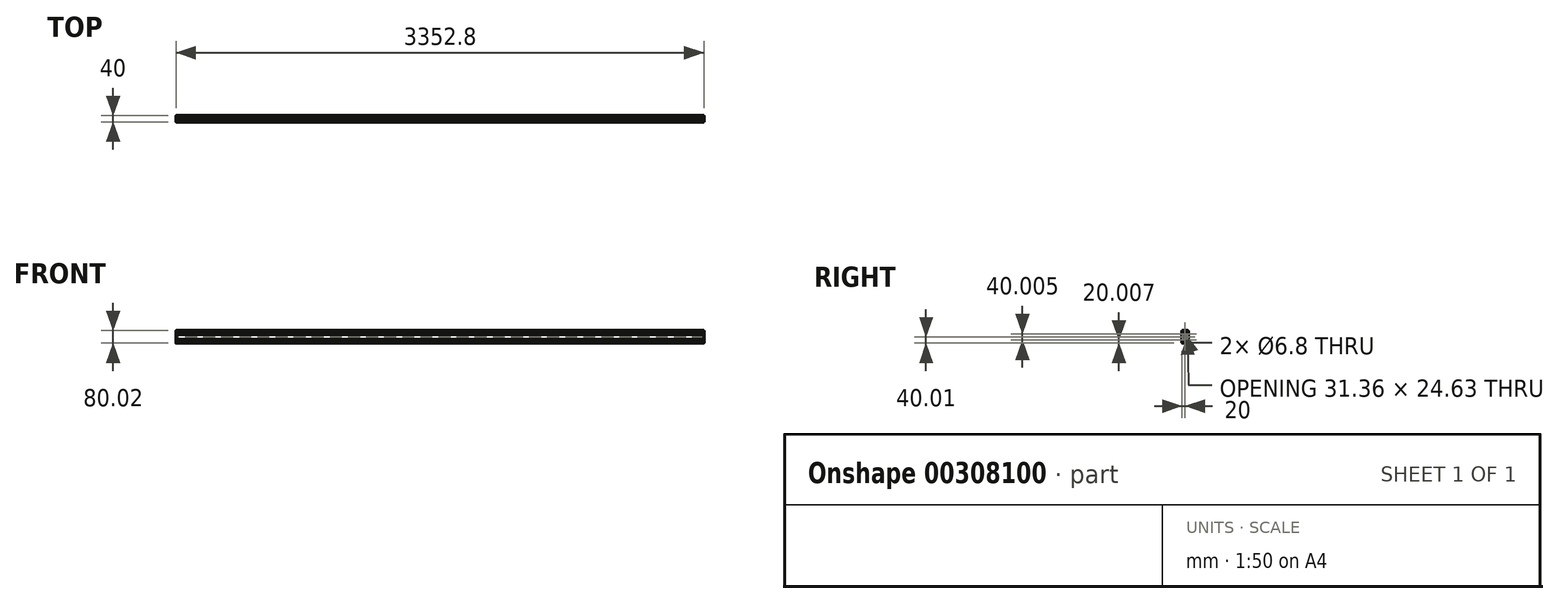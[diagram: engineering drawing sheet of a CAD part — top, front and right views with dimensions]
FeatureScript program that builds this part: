
annotation { "Feature Type Name" : "Feature", "Feature Type Description" : "" }
export const myFeature = defineFeature(function(context is Context, id is Id, definition is map)
    precondition{}
    {
        {
            var Q0;
            Q0=qCreatedBy(makeId("Right.planeOp"),FACE);
            var sketch = newSketch(context, id + "F0", { "sketchPlane" : qUnion([Q0])});
            skLineSegment(sketch, "E0", {"start": v(-3.57, -20) * mm, "end": v(3.57, -20) * mm});
            skLineSegment(sketch, "E1", {"start": v(0, -23.57) * mm, "end": v(0, -16.43) * mm});
            skLineSegment(sketch, "E2", {"start": v(-3.57, 20) * mm, "end": v(3.57, 20) * mm});
            skLineSegment(sketch, "E3", {"start": v(0, 16.43) * mm, "end": v(0, 23.57) * mm});
            skArc(sketch, "E4", {"start": v(-16.83, 40) * mm, "mid": v(-19.07, 39.08) * mm, "end": v(-20, 36.83) * mm});
            skLineSegment(sketch, "E5", {"start": v(-20, 36.83) * mm, "end": v(-20, 25.7) * mm});
            skArc(sketch, "E6", {"start": v(-20, 25.7) * mm, "mid": v(-19.54, 24.58) * mm, "end": v(-18.43, 24.12) * mm});
            skLineSegment(sketch, "E7", {"start": v(-18.43, 24.12) * mm, "end": v(-17.25, 24.12) * mm});
            skArc(sketch, "E8", {"start": v(-17.25, 24.12) * mm, "mid": v(-16.14, 24.58) * mm, "end": v(-15.68, 25.7) * mm});
            skLineSegment(sketch, "E9", {"start": v(-15.68, 25.7) * mm, "end": v(-15.68, 28.72) * mm});
            skArc(sketch, "E10", {"start": v(-14.11, 30.29) * mm, "mid": v(-15.22, 29.83) * mm, "end": v(-15.68, 28.72) * mm});
            skLineSegment(sketch, "E11", {"start": v(-14.11, 30.29) * mm, "end": v(-13.66, 30.29) * mm});
            skArc(sketch, "E12", {"start": v(-13.12, 30.07) * mm, "mid": v(-13.37, 30.23) * mm, "end": v(-13.66, 30.29) * mm});
            skLineSegment(sketch, "E13", {"start": v(-13.12, 30.07) * mm, "end": v(-9.11, 26.06) * mm});
            skArc(sketch, "E14", {"start": v(-7.69, 22.62) * mm, "mid": v(-8.06, 24.48) * mm, "end": v(-9.11, 26.06) * mm});
            skLineSegment(sketch, "E15", {"start": v(-7.69, 22.62) * mm, "end": v(-7.69, 17.39) * mm});
            skArc(sketch, "E16", {"start": v(-9.11, 13.95) * mm, "mid": v(-8.06, 15.53) * mm, "end": v(-7.69, 17.39) * mm});
            skLineSegment(sketch, "E17", {"start": v(-9.11, 13.95) * mm, "end": v(-13.12, 9.94) * mm});
            skArc(sketch, "E18", {"start": v(-13.66, 9.72) * mm, "mid": v(-13.37, 9.77) * mm, "end": v(-13.12, 9.94) * mm});
            skLineSegment(sketch, "E19", {"start": v(-13.66, 9.72) * mm, "end": v(-14.11, 9.72) * mm});
            skArc(sketch, "E20", {"start": v(-15.68, 11.29) * mm, "mid": v(-15.22, 10.18) * mm, "end": v(-14.11, 9.72) * mm});
            skLineSegment(sketch, "E21", {"start": v(-15.68, 11.29) * mm, "end": v(-15.68, 14.31) * mm});
            skArc(sketch, "E22", {"start": v(-15.68, 14.31) * mm, "mid": v(-16.14, 15.42) * mm, "end": v(-17.25, 15.88) * mm});
            skLineSegment(sketch, "E23", {"start": v(-17.25, 15.88) * mm, "end": v(-18.43, 15.88) * mm});
            skArc(sketch, "E24", {"start": v(-18.43, 15.88) * mm, "mid": v(-19.54, 15.42) * mm, "end": v(-20, 14.31) * mm});
            skLineSegment(sketch, "E25", {"start": v(-20, 14.31) * mm, "end": v(-20, -14.31) * mm});
            skArc(sketch, "E26", {"start": v(-20, -14.31) * mm, "mid": v(-19.54, -15.42) * mm, "end": v(-18.43, -15.88) * mm});
            skLineSegment(sketch, "E27", {"start": v(-18.43, -15.88) * mm, "end": v(-17.25, -15.88) * mm});
            skArc(sketch, "E28", {"start": v(-17.25, -15.88) * mm, "mid": v(-16.14, -15.42) * mm, "end": v(-15.68, -14.31) * mm});
            skLineSegment(sketch, "E29", {"start": v(-15.68, -14.31) * mm, "end": v(-15.68, -11.29) * mm});
            skArc(sketch, "E30", {"start": v(-14.11, -9.72) * mm, "mid": v(-15.22, -10.18) * mm, "end": v(-15.68, -11.29) * mm});
            skLineSegment(sketch, "E31", {"start": v(-14.11, -9.72) * mm, "end": v(-13.66, -9.72) * mm});
            skArc(sketch, "E32", {"start": v(-13.12, -9.94) * mm, "mid": v(-13.37, -9.77) * mm, "end": v(-13.66, -9.72) * mm});
            skLineSegment(sketch, "E33", {"start": v(-13.12, -9.94) * mm, "end": v(-9.11, -13.95) * mm});
            skArc(sketch, "E34", {"start": v(-7.69, -17.39) * mm, "mid": v(-8.06, -15.53) * mm, "end": v(-9.11, -13.95) * mm});
            skLineSegment(sketch, "E35", {"start": v(-7.69, -17.39) * mm, "end": v(-7.69, -22.62) * mm});
            skArc(sketch, "E36", {"start": v(-9.11, -26.06) * mm, "mid": v(-8.06, -24.48) * mm, "end": v(-7.69, -22.62) * mm});
            skLineSegment(sketch, "E37", {"start": v(-9.11, -26.06) * mm, "end": v(-13.12, -30.07) * mm});
            skArc(sketch, "E38", {"start": v(-13.66, -30.29) * mm, "mid": v(-13.37, -30.23) * mm, "end": v(-13.12, -30.07) * mm});
            skLineSegment(sketch, "E39", {"start": v(-13.66, -30.29) * mm, "end": v(-14.11, -30.29) * mm});
            skArc(sketch, "E40", {"start": v(-15.68, -28.72) * mm, "mid": v(-15.22, -29.83) * mm, "end": v(-14.11, -30.29) * mm});
            skLineSegment(sketch, "E41", {"start": v(-15.68, -28.72) * mm, "end": v(-15.68, -25.7) * mm});
            skArc(sketch, "E42", {"start": v(-15.68, -25.7) * mm, "mid": v(-16.14, -24.58) * mm, "end": v(-17.25, -24.12) * mm});
            skLineSegment(sketch, "E43", {"start": v(-17.25, -24.12) * mm, "end": v(-18.43, -24.12) * mm});
            skArc(sketch, "E44", {"start": v(-18.43, -24.12) * mm, "mid": v(-19.54, -24.58) * mm, "end": v(-20, -25.7) * mm});
            skLineSegment(sketch, "E45", {"start": v(-20, -25.7) * mm, "end": v(-20, -36.83) * mm});
            skArc(sketch, "E46", {"start": v(-20, -36.83) * mm, "mid": v(-19.07, -39.08) * mm, "end": v(-16.83, -40) * mm});
            skLineSegment(sketch, "E47", {"start": v(-16.83, -40) * mm, "end": v(-5.7, -40) * mm});
            skArc(sketch, "E48", {"start": v(-5.7, -40) * mm, "mid": v(-4.58, -39.55) * mm, "end": v(-4.12, -38.43) * mm});
            skLineSegment(sketch, "E49", {"start": v(-4.12, -38.43) * mm, "end": v(-4.12, -37.25) * mm});
            skArc(sketch, "E50", {"start": v(-4.12, -37.25) * mm, "mid": v(-4.58, -36.14) * mm, "end": v(-5.7, -35.68) * mm});
            skLineSegment(sketch, "E51", {"start": v(-5.7, -35.68) * mm, "end": v(-8.72, -35.68) * mm});
            skArc(sketch, "E52", {"start": v(-10.29, -34.11) * mm, "mid": v(-9.83, -35.22) * mm, "end": v(-8.72, -35.68) * mm});
            skLineSegment(sketch, "E53", {"start": v(-10.29, -34.11) * mm, "end": v(-10.29, -33.66) * mm});
            skArc(sketch, "E54", {"start": v(-10.06, -33.12) * mm, "mid": v(-10.23, -33.37) * mm, "end": v(-10.29, -33.66) * mm});
            skLineSegment(sketch, "E55", {"start": v(-10.06, -33.12) * mm, "end": v(-6.06, -29.11) * mm});
            skArc(sketch, "E56", {"start": v(-2.62, -27.69) * mm, "mid": v(-4.48, -28.06) * mm, "end": v(-6.06, -29.11) * mm});
            skLineSegment(sketch, "E57", {"start": v(-2.62, -27.69) * mm, "end": v(2.62, -27.69) * mm});
            skArc(sketch, "E58", {"start": v(6.06, -29.11) * mm, "mid": v(4.48, -28.06) * mm, "end": v(2.62, -27.69) * mm});
            skLineSegment(sketch, "E59", {"start": v(6.06, -29.11) * mm, "end": v(10.06, -33.12) * mm});
            skArc(sketch, "E60", {"start": v(10.29, -33.66) * mm, "mid": v(10.23, -33.37) * mm, "end": v(10.06, -33.12) * mm});
            skLineSegment(sketch, "E61", {"start": v(10.29, -33.66) * mm, "end": v(10.29, -34.11) * mm});
            skArc(sketch, "E62", {"start": v(8.72, -35.68) * mm, "mid": v(9.83, -35.22) * mm, "end": v(10.29, -34.11) * mm});
            skLineSegment(sketch, "E63", {"start": v(8.72, -35.68) * mm, "end": v(5.7, -35.68) * mm});
            skArc(sketch, "E64", {"start": v(5.7, -35.68) * mm, "mid": v(4.58, -36.14) * mm, "end": v(4.12, -37.25) * mm});
            skLineSegment(sketch, "E65", {"start": v(4.12, -37.25) * mm, "end": v(4.12, -38.43) * mm});
            skArc(sketch, "E66", {"start": v(4.12, -38.43) * mm, "mid": v(4.58, -39.55) * mm, "end": v(5.7, -40) * mm});
            skLineSegment(sketch, "E67", {"start": v(5.7, -40) * mm, "end": v(16.83, -40) * mm});
            skArc(sketch, "E68", {"start": v(16.83, -40) * mm, "mid": v(19.07, -39.08) * mm, "end": v(20, -36.83) * mm});
            skLineSegment(sketch, "E69", {"start": v(20, -36.83) * mm, "end": v(20, -25.7) * mm});
            skArc(sketch, "E70", {"start": v(20, -25.7) * mm, "mid": v(19.54, -24.58) * mm, "end": v(18.43, -24.12) * mm});
            skLineSegment(sketch, "E71", {"start": v(18.43, -24.12) * mm, "end": v(17.25, -24.12) * mm});
            skArc(sketch, "E72", {"start": v(17.25, -24.12) * mm, "mid": v(16.14, -24.58) * mm, "end": v(15.68, -25.7) * mm});
            skLineSegment(sketch, "E73", {"start": v(15.68, -25.7) * mm, "end": v(15.68, -28.72) * mm});
            skArc(sketch, "E74", {"start": v(14.11, -30.29) * mm, "mid": v(15.22, -29.83) * mm, "end": v(15.68, -28.72) * mm});
            skLineSegment(sketch, "E75", {"start": v(14.11, -30.29) * mm, "end": v(13.66, -30.29) * mm});
            skArc(sketch, "E76", {"start": v(13.12, -30.07) * mm, "mid": v(13.37, -30.23) * mm, "end": v(13.66, -30.29) * mm});
            skLineSegment(sketch, "E77", {"start": v(13.12, -30.07) * mm, "end": v(9.11, -26.06) * mm});
            skArc(sketch, "E78", {"start": v(7.69, -22.62) * mm, "mid": v(8.06, -24.48) * mm, "end": v(9.11, -26.06) * mm});
            skLineSegment(sketch, "E79", {"start": v(7.69, -22.62) * mm, "end": v(7.69, -17.39) * mm});
            skArc(sketch, "E80", {"start": v(9.11, -13.95) * mm, "mid": v(8.06, -15.53) * mm, "end": v(7.69, -17.39) * mm});
            skLineSegment(sketch, "E81", {"start": v(9.11, -13.95) * mm, "end": v(13.12, -9.94) * mm});
            skArc(sketch, "E82", {"start": v(13.66, -9.72) * mm, "mid": v(13.37, -9.77) * mm, "end": v(13.12, -9.94) * mm});
            skLineSegment(sketch, "E83", {"start": v(13.66, -9.72) * mm, "end": v(14.11, -9.72) * mm});
            skArc(sketch, "E84", {"start": v(15.68, -11.29) * mm, "mid": v(15.22, -10.18) * mm, "end": v(14.11, -9.72) * mm});
            skLineSegment(sketch, "E85", {"start": v(15.68, -11.29) * mm, "end": v(15.68, -14.31) * mm});
            skArc(sketch, "E86", {"start": v(15.68, -14.31) * mm, "mid": v(16.14, -15.42) * mm, "end": v(17.25, -15.88) * mm});
            skLineSegment(sketch, "E87", {"start": v(17.25, -15.88) * mm, "end": v(18.43, -15.88) * mm});
            skArc(sketch, "E88", {"start": v(18.43, -15.88) * mm, "mid": v(19.54, -15.42) * mm, "end": v(20, -14.31) * mm});
            skLineSegment(sketch, "E89", {"start": v(20, -14.31) * mm, "end": v(20, 14.31) * mm});
            skArc(sketch, "E90", {"start": v(20, 14.31) * mm, "mid": v(19.54, 15.42) * mm, "end": v(18.43, 15.88) * mm});
            skLineSegment(sketch, "E91", {"start": v(18.43, 15.88) * mm, "end": v(17.25, 15.88) * mm});
            skArc(sketch, "E92", {"start": v(17.25, 15.88) * mm, "mid": v(16.14, 15.42) * mm, "end": v(15.68, 14.31) * mm});
            skLineSegment(sketch, "E93", {"start": v(15.68, 14.31) * mm, "end": v(15.68, 11.29) * mm});
            skArc(sketch, "E94", {"start": v(14.11, 9.72) * mm, "mid": v(15.22, 10.18) * mm, "end": v(15.68, 11.29) * mm});
            skLineSegment(sketch, "E95", {"start": v(14.11, 9.72) * mm, "end": v(13.66, 9.72) * mm});
            skArc(sketch, "E96", {"start": v(13.12, 9.94) * mm, "mid": v(13.37, 9.77) * mm, "end": v(13.66, 9.72) * mm});
            skLineSegment(sketch, "E97", {"start": v(13.12, 9.94) * mm, "end": v(9.11, 13.95) * mm});
            skArc(sketch, "E98", {"start": v(7.69, 17.39) * mm, "mid": v(8.06, 15.53) * mm, "end": v(9.11, 13.95) * mm});
            skLineSegment(sketch, "E99", {"start": v(7.69, 17.39) * mm, "end": v(7.69, 22.62) * mm});
            skArc(sketch, "E100", {"start": v(9.11, 26.06) * mm, "mid": v(8.06, 24.48) * mm, "end": v(7.69, 22.62) * mm});
            skLineSegment(sketch, "E101", {"start": v(9.11, 26.06) * mm, "end": v(13.12, 30.07) * mm});
            skArc(sketch, "E102", {"start": v(13.66, 30.29) * mm, "mid": v(13.37, 30.23) * mm, "end": v(13.12, 30.07) * mm});
            skLineSegment(sketch, "E103", {"start": v(13.66, 30.29) * mm, "end": v(14.11, 30.29) * mm});
            skArc(sketch, "E104", {"start": v(15.68, 28.72) * mm, "mid": v(15.22, 29.83) * mm, "end": v(14.11, 30.29) * mm});
            skLineSegment(sketch, "E105", {"start": v(15.68, 28.72) * mm, "end": v(15.68, 25.7) * mm});
            skArc(sketch, "E106", {"start": v(15.68, 25.7) * mm, "mid": v(16.14, 24.58) * mm, "end": v(17.25, 24.12) * mm});
            skLineSegment(sketch, "E107", {"start": v(17.25, 24.12) * mm, "end": v(18.43, 24.12) * mm});
            skArc(sketch, "E108", {"start": v(18.43, 24.12) * mm, "mid": v(19.54, 24.58) * mm, "end": v(20, 25.7) * mm});
            skLineSegment(sketch, "E109", {"start": v(20, 25.7) * mm, "end": v(20, 36.83) * mm});
            skArc(sketch, "E110", {"start": v(20, 36.83) * mm, "mid": v(19.07, 39.08) * mm, "end": v(16.83, 40) * mm});
            skLineSegment(sketch, "E111", {"start": v(16.83, 40) * mm, "end": v(5.7, 40) * mm});
            skArc(sketch, "E112", {"start": v(5.7, 40) * mm, "mid": v(4.58, 39.55) * mm, "end": v(4.12, 38.43) * mm});
            skLineSegment(sketch, "E113", {"start": v(4.12, 38.43) * mm, "end": v(4.12, 37.25) * mm});
            skArc(sketch, "E114", {"start": v(4.12, 37.25) * mm, "mid": v(4.58, 36.14) * mm, "end": v(5.7, 35.68) * mm});
            skLineSegment(sketch, "E115", {"start": v(5.7, 35.68) * mm, "end": v(8.72, 35.68) * mm});
            skArc(sketch, "E116", {"start": v(10.29, 34.11) * mm, "mid": v(9.83, 35.22) * mm, "end": v(8.72, 35.68) * mm});
            skLineSegment(sketch, "E117", {"start": v(10.29, 34.11) * mm, "end": v(10.29, 33.66) * mm});
            skArc(sketch, "E118", {"start": v(10.06, 33.12) * mm, "mid": v(10.23, 33.37) * mm, "end": v(10.29, 33.66) * mm});
            skLineSegment(sketch, "E119", {"start": v(10.06, 33.12) * mm, "end": v(6.06, 29.11) * mm});
            skArc(sketch, "E120", {"start": v(2.62, 27.69) * mm, "mid": v(4.48, 28.06) * mm, "end": v(6.06, 29.11) * mm});
            skLineSegment(sketch, "E121", {"start": v(2.62, 27.69) * mm, "end": v(-2.62, 27.69) * mm});
            skArc(sketch, "E122", {"start": v(-6.06, 29.11) * mm, "mid": v(-4.48, 28.06) * mm, "end": v(-2.62, 27.69) * mm});
            skLineSegment(sketch, "E123", {"start": v(-6.06, 29.11) * mm, "end": v(-10.06, 33.12) * mm});
            skArc(sketch, "E124", {"start": v(-10.29, 33.66) * mm, "mid": v(-10.23, 33.37) * mm, "end": v(-10.06, 33.12) * mm});
            skLineSegment(sketch, "E125", {"start": v(-10.29, 33.66) * mm, "end": v(-10.29, 34.11) * mm});
            skArc(sketch, "E126", {"start": v(-8.72, 35.68) * mm, "mid": v(-9.83, 35.22) * mm, "end": v(-10.29, 34.11) * mm});
            skLineSegment(sketch, "E127", {"start": v(-8.72, 35.68) * mm, "end": v(-5.7, 35.68) * mm});
            skArc(sketch, "E128", {"start": v(-5.7, 35.68) * mm, "mid": v(-4.58, 36.14) * mm, "end": v(-4.12, 37.25) * mm});
            skLineSegment(sketch, "E129", {"start": v(-4.12, 37.25) * mm, "end": v(-4.12, 38.43) * mm});
            skArc(sketch, "E130", {"start": v(-4.12, 38.43) * mm, "mid": v(-4.58, 39.55) * mm, "end": v(-5.7, 40) * mm});
            skLineSegment(sketch, "E131", {"start": v(-15.68, 4.07) * mm, "end": v(-15.68, -4.07) * mm});
            skArc(sketch, "E132", {"start": v(-14.41, 5.34) * mm, "mid": v(-15.3, 4.97) * mm, "end": v(-15.68, 4.07) * mm});
            skLineSegment(sketch, "E133", {"start": v(-12.13, 5.34) * mm, "end": v(-14.41, 5.34) * mm});
            skArc(sketch, "E134", {"start": v(-12.13, 5.34) * mm, "mid": v(-11.65, 5.44) * mm, "end": v(-11.23, 5.71) * mm});
            skLineSegment(sketch, "E135", {"start": v(-6.06, 10.9) * mm, "end": v(-11.23, 5.71) * mm});
            skArc(sketch, "E136", {"start": v(-2.62, 12.32) * mm, "mid": v(-4.48, 11.95) * mm, "end": v(-6.06, 10.9) * mm});
            skLineSegment(sketch, "E137", {"start": v(2.62, 12.32) * mm, "end": v(-2.62, 12.32) * mm});
            skArc(sketch, "E138", {"start": v(6.06, 10.9) * mm, "mid": v(4.48, 11.95) * mm, "end": v(2.62, 12.32) * mm});
            skLineSegment(sketch, "E139", {"start": v(11.23, 5.71) * mm, "end": v(6.06, 10.9) * mm});
            skArc(sketch, "E140", {"start": v(11.23, 5.71) * mm, "mid": v(11.65, 5.44) * mm, "end": v(12.13, 5.34) * mm});
            skLineSegment(sketch, "E141", {"start": v(14.41, 5.34) * mm, "end": v(12.13, 5.34) * mm});
            skArc(sketch, "E142", {"start": v(15.68, 4.07) * mm, "mid": v(15.3, 4.97) * mm, "end": v(14.41, 5.34) * mm});
            skLineSegment(sketch, "E143", {"start": v(15.68, -4.07) * mm, "end": v(15.68, 4.07) * mm});
            skArc(sketch, "E144", {"start": v(14.41, -5.34) * mm, "mid": v(15.3, -4.97) * mm, "end": v(15.68, -4.07) * mm});
            skLineSegment(sketch, "E145", {"start": v(12.13, -5.34) * mm, "end": v(14.41, -5.34) * mm});
            skArc(sketch, "E146", {"start": v(12.13, -5.34) * mm, "mid": v(11.65, -5.44) * mm, "end": v(11.23, -5.71) * mm});
            skLineSegment(sketch, "E147", {"start": v(6.06, -10.9) * mm, "end": v(11.23, -5.71) * mm});
            skArc(sketch, "E148", {"start": v(2.62, -12.32) * mm, "mid": v(4.48, -11.95) * mm, "end": v(6.06, -10.9) * mm});
            skLineSegment(sketch, "E149", {"start": v(-2.62, -12.32) * mm, "end": v(2.62, -12.32) * mm});
            skArc(sketch, "E150", {"start": v(-6.06, -10.9) * mm, "mid": v(-4.48, -11.95) * mm, "end": v(-2.62, -12.32) * mm});
            skLineSegment(sketch, "E151", {"start": v(-11.23, -5.71) * mm, "end": v(-6.06, -10.9) * mm});
            skArc(sketch, "E152", {"start": v(-11.23, -5.71) * mm, "mid": v(-11.65, -5.44) * mm, "end": v(-12.13, -5.34) * mm});
            skLineSegment(sketch, "E153", {"start": v(-14.41, -5.34) * mm, "end": v(-12.13, -5.34) * mm});
            skCircle(sketch, "E154", {"center": v(0, -20) * mm, "radius": 3.4 * mm});
            skCircle(sketch, "E155", {"center": v(0, 20) * mm, "radius": 3.4 * mm});
            skArc(sketch, "E156", {"start": v(-15.68, -4.07) * mm, "mid": v(-15.3, -4.97) * mm, "end": v(-14.41, -5.34) * mm});
            skLineSegment(sketch, "E157", {"start": v(-5.7, 40) * mm, "end": v(-16.83, 40) * mm});
            skSolve(sketch);
        }
        {
            var Q0;
            Q0 = qSketchRegion(id + "F0", true);
            extrude(context, id + "F1", {"entities" : qUnion([Q0]), "endBound" : BoundingType.SYMMETRIC, "depth" : 3352.8 * mm});
        }
    });
